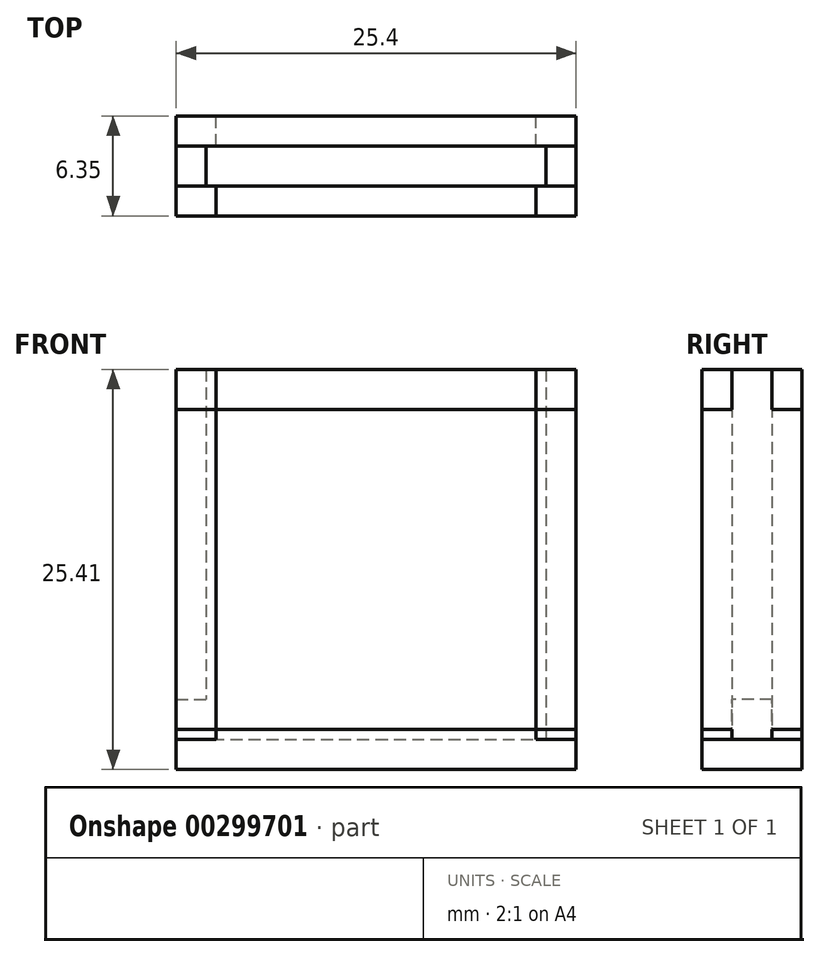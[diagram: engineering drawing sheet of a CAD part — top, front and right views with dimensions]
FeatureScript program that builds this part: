
annotation { "Feature Type Name" : "Feature", "Feature Type Description" : "" }
export const myFeature = defineFeature(function(context is Context, id is Id, definition is map)
    precondition{}
    {
        {
            var Q0;
            Q0=qCreatedBy(makeId("Front.planeOp"),FACE);
            var sketch = newSketch(context, id + "F0", { "sketchPlane" : qUnion([Q0])});
            skLineSegment(sketch, "E0.top", {"start": v(-12.7, -1.9) * mm, "end": v(12.7, -1.9) * mm});
            skPoint(sketch, "E0.middle", {"position": v(0, 0) * mm});
            skLineSegment(sketch, "E1", {"start": v(10.8, 21.6) * mm, "end": v(10.8, 0) * mm});
            skLineSegment(sketch, "E2", {"start": v(-10.8, 21.6) * mm, "end": v(-10.8, 0) * mm});
            skLineSegment(sketch, "E3.top", {"start": v(-12.7, 23.5) * mm, "end": v(12.7, 23.5) * mm});
            skLineSegment(sketch, "E4", {"start": v(-10.8, 21.6) * mm, "end": v(10.8, 21.6) * mm});
            skLineSegment(sketch, "E5", {"start": v(-10.8, 0) * mm, "end": v(10.8, 0) * mm});
            skLineSegment(sketch, "E6", {"start": v(-12.7, -1.9) * mm, "end": v(-12.7, 23.5) * mm});
            skLineSegment(sketch, "E7", {"start": v(12.7, -1.9) * mm, "end": v(12.7, 23.5) * mm});
            skSolve(sketch);
        }
        {
            var Q0;
            Q0=qCreatedBy(makeId("Right.planeOp"),FACE);
            var sketch = newSketch(context, id + "F1", { "sketchPlane" : qUnion([Q0])});
            skLineSegment(sketch, "E8.bottom", {"start": v(8.57, 23.5) * mm, "end": v(10.48, 23.5) * mm});
            skLineSegment(sketch, "E8.left", {"start": v(8.57, 23.5) * mm, "end": v(8.57, 23.5) * mm});
            skLineSegment(sketch, "E8.right", {"start": v(10.48, 23.5) * mm, "end": v(10.36, -1.9) * mm});
            skLineSegment(sketch, "E9", {"start": v(8.57, -1.9) * mm, "end": v(10.36, -1.9) * mm});
            skLineSegment(sketch, "E10.bottom", {"start": v(-8.57, 0.63) * mm, "end": v(-10.48, 0.63) * mm});
            skLineSegment(sketch, "E10.left", {"start": v(-8.57, 0.63) * mm, "end": v(-8.57, -1.9) * mm});
            skLineSegment(sketch, "E11.right", {"start": v(-14.92, 0.63) * mm, "end": v(-14.92, -1.9) * mm});
            skLineSegment(sketch, "E12", {"start": v(-14.92, 20.96) * mm, "end": v(-14.92, 23.5) * mm});
            skLineSegment(sketch, "E13", {"start": v(-8.57, 23.5) * mm, "end": v(-8.57, 20.96) * mm});
            skLineSegment(sketch, "E14", {"start": v(-8.57, 20.96) * mm, "end": v(-10.48, 20.95) * mm});
            skLineSegment(sketch, "E15", {"start": v(-10.48, 20.95) * mm, "end": v(-10.48, 23.5) * mm});
            skLineSegment(sketch, "E16", {"start": v(-13.02, 23.5) * mm, "end": v(-13.02, 20.96) * mm});
            skLineSegment(sketch, "E17", {"start": v(-13.02, 20.96) * mm, "end": v(-14.92, 20.96) * mm});
            skLineSegment(sketch, "E18", {"start": v(-13.02, 23.5) * mm, "end": v(-14.92, 23.5) * mm});
            skLineSegment(sketch, "E19", {"start": v(-8.57, 23.5) * mm, "end": v(-10.48, 23.5) * mm});
            skLineSegment(sketch, "E20", {"start": v(-14.92, -1.9) * mm, "end": v(-8.57, -1.9) * mm});
            skLineSegment(sketch, "E21", {"start": v(-10.48, 0.63) * mm, "end": v(-10.48, 0) * mm});
            skLineSegment(sketch, "E22", {"start": v(-10.48, 0) * mm, "end": v(-13.02, 0) * mm});
            skLineSegment(sketch, "E23", {"start": v(-13.02, 0) * mm, "end": v(-13.02, 0.63) * mm});
            skLineSegment(sketch, "E24", {"start": v(-13.02, 0.63) * mm, "end": v(-14.92, 0.63) * mm});
            skLineSegment(sketch, "E25", {"start": v(8.57, -1.9) * mm, "end": v(8.57, 23.5) * mm});
            skSolve(sketch);
        }
        {
            var Q0;
            Q0=makeQuery(id+"F1.imprint","IMPRINT",FACE,{"disambiguationData":[TD([[makeQuery(id+"F1.imprint","IMPRINT",EDGE,{"derivedFrom":sQuery(id+"F1.wireOp",EDGE,"E10.bottom")}),1.0]])]});
            var Q1;
            Q1=makeQuery(id+"F1.imprint","IMPRINT",FACE,{"disambiguationData":[TD([[makeQuery(id+"F1.imprint","IMPRINT",EDGE,{"derivedFrom":sQuery(id+"F1.wireOp",EDGE,"E12")}),-1.0]])]});
            var Q2;
            Q2=makeQuery(id+"F1.imprint","IMPRINT",FACE,{"disambiguationData":[TD([[makeQuery(id+"F1.imprint","IMPRINT",EDGE,{"derivedFrom":sQuery(id+"F1.wireOp",EDGE,"E13")}),-1.0]])]});
            extrude(context, id + "F2", {"entities" : qUnion([Q0, Q1, Q2]), "endBound" : BoundingType.SYMMETRIC, "depth" : 25.4 * mm});
        }
        {
            var Q0;
            Q0=qCreatedBy(makeId("Top.planeOp"),FACE);
            var sketch = newSketch(context, id + "F3", { "sketchPlane" : qUnion([Q0])});
            skLineSegment(sketch, "E26", {"start": v(-12.7, -8.57) * mm, "end": v(-12.7, -14.92) * mm});
            skLineSegment(sketch, "E27", {"start": v(-12.7, -14.92) * mm, "end": v(-10.16, -14.92) * mm});
            skLineSegment(sketch, "E28", {"start": v(-10.16, -14.92) * mm, "end": v(-10.16, -13.02) * mm});
            skLineSegment(sketch, "E29", {"start": v(-10.16, -13.02) * mm, "end": v(-10.8, -13.02) * mm});
            skLineSegment(sketch, "E30", {"start": v(-10.8, -13.02) * mm, "end": v(-10.8, -10.48) * mm});
            skLineSegment(sketch, "E31", {"start": v(-10.8, -10.48) * mm, "end": v(-10.16, -10.48) * mm});
            skLineSegment(sketch, "E32", {"start": v(-10.16, -10.48) * mm, "end": v(-10.16, -8.57) * mm});
            skLineSegment(sketch, "E33", {"start": v(-10.16, -8.57) * mm, "end": v(-12.7, -8.57) * mm});
            skLineSegment(sketch, "E34.MirrorCS", {"start": v(10.16, -8.57) * mm, "end": v(12.7, -8.57) * mm});
            skLineSegment(sketch, "E35.MirrorCS", {"start": v(10.16, -10.48) * mm, "end": v(10.16, -8.57) * mm});
            skLineSegment(sketch, "E36.MirrorCS", {"start": v(10.8, -10.48) * mm, "end": v(10.16, -10.48) * mm});
            skLineSegment(sketch, "E37.MirrorCS", {"start": v(10.8, -13.02) * mm, "end": v(10.8, -10.48) * mm});
            skLineSegment(sketch, "E38.MirrorCS", {"start": v(10.16, -13.02) * mm, "end": v(10.8, -13.02) * mm});
            skLineSegment(sketch, "E39.MirrorCS", {"start": v(10.16, -14.92) * mm, "end": v(10.16, -13.02) * mm});
            skLineSegment(sketch, "E40.MirrorCS", {"start": v(12.7, -8.57) * mm, "end": v(12.7, -14.92) * mm});
            skLineSegment(sketch, "E41.MirrorCS", {"start": v(12.7, -14.92) * mm, "end": v(10.16, -14.92) * mm});
            skSolve(sketch);
        }
        {
            var Q0;
            Q0=makeQuery(id+"F3.imprint","IMPRINT",FACE,{"disambiguationData":[TD([[makeQuery(id+"F3.imprint","IMPRINT",EDGE,{"derivedFrom":sQuery(id+"F3.wireOp",EDGE,"E26")}),1.0]])]});
            var Q1;
            Q1=makeQuery(id+"F3.imprint","IMPRINT",FACE,{"disambiguationData":[TD([[makeQuery(id+"F3.imprint","IMPRINT",EDGE,{"derivedFrom":sQuery(id+"F3.wireOp",EDGE,"E34.MirrorCS")}),-1.0]])]});
            extrude(context, id + "F4", {"entities" : qUnion([Q0, Q1]), "depth" : 23.5 * mm});
        }
        {
            var Q0;
            Q0=qCreatedBy(makeId("Right.planeOp"),FACE);
            var sketch = newSketch(context, id + "F5", { "sketchPlane" : qUnion([Q0])});
            skLineSegment(sketch, "E42.bottom", {"start": v(-10.48, 0) * mm, "end": v(-13.02, 0) * mm});
            skLineSegment(sketch, "E42.top", {"start": v(-10.48, 2.54) * mm, "end": v(-13.02, 2.54) * mm});
            skLineSegment(sketch, "E42.left", {"start": v(-10.48, 0) * mm, "end": v(-10.48, 2.54) * mm});
            skLineSegment(sketch, "E42.right", {"start": v(-13.02, 0) * mm, "end": v(-13.02, 2.54) * mm});
            skSolve(sketch);
        }
        {
            var Q0;
            Q0=qSketchRegion(id+"F5",true);
            extrude(context, id + "F6", {"entities" : qUnion([Q0]), "operationType" : NewBodyOperationType.REMOVE, "oppositeDirection" : true, "depth" : 12.7 * mm});
        }
    });
